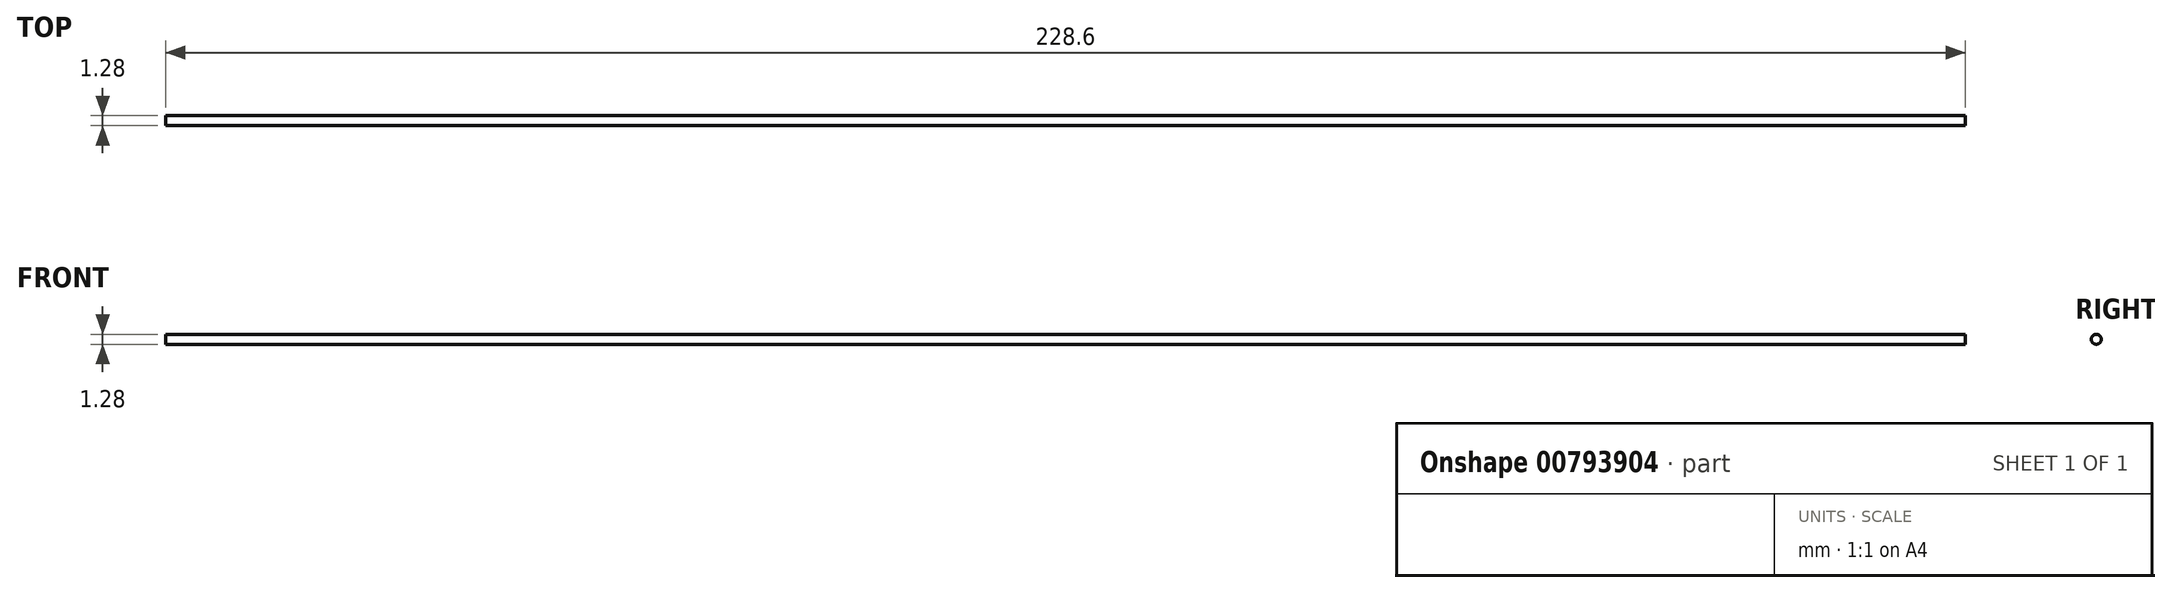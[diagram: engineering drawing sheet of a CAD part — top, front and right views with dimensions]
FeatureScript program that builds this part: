
annotation { "Feature Type Name" : "Feature", "Feature Type Description" : "" }
export const myFeature = defineFeature(function(context is Context, id is Id, definition is map)
    precondition{}
    {
        {
            var Q0;
            Q0=qCreatedBy(makeId("Right.planeOp"),FACE);
            var sketch = newSketch(context, id + "F0", { "sketchPlane" : qUnion([Q0])});
            skCircle(sketch, "E0", {"center": v(0, 0) * mm, "radius": 0.64 * mm});
            skSolve(sketch);
        }
        {
            var Q0;
            Q0=qSketchRegion(id+"F0",true);
            extrude(context, id + "F1", {"entities" : qUnion([Q0]), "endBound" : BoundingType.SYMMETRIC, "depth" : 228.6 * mm, "offsetDistance" : 25.4 * mm});
        }
    });
